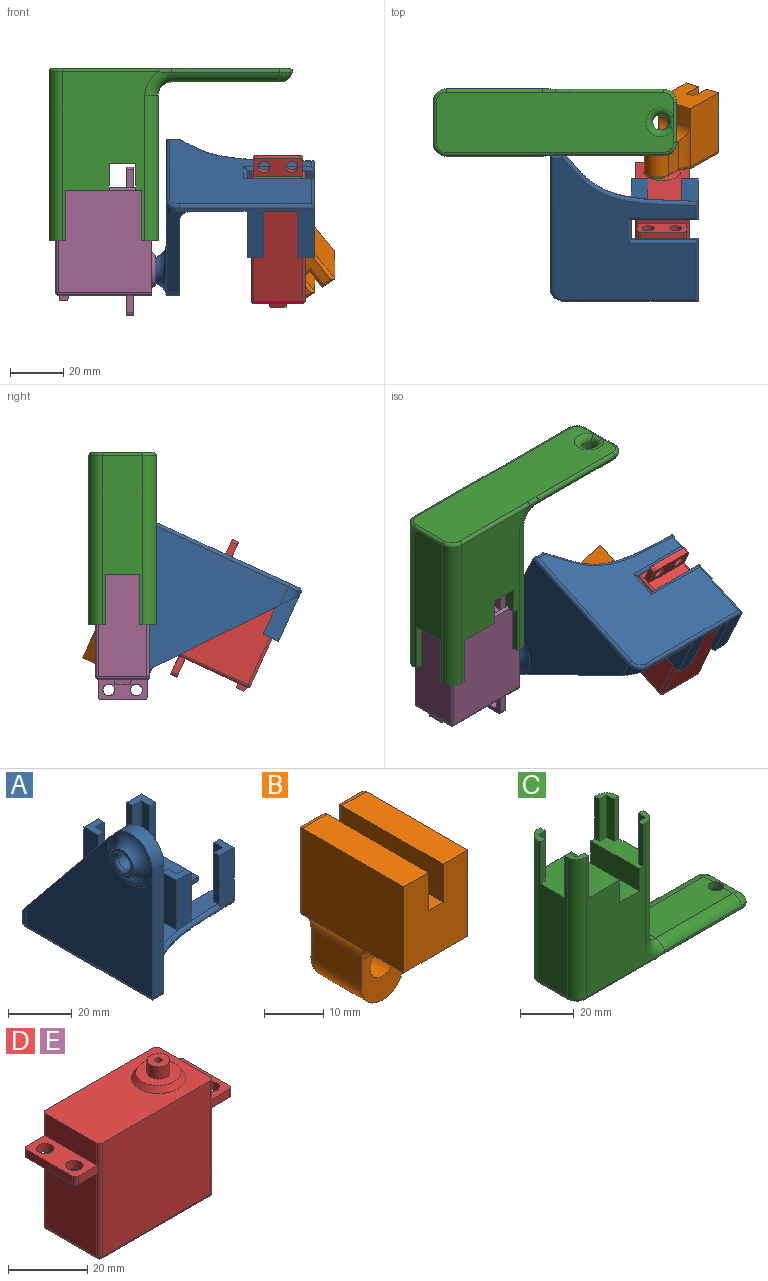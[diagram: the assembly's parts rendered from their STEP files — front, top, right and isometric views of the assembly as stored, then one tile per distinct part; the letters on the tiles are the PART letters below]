
ASSEMBLY  parts=5 mates=3
PART A: 56 faces, bbox 65.1x64.5x63.1 mm
  f0: plane 58.3x53.35mm, normal (0,0,-1), area 2065.8mm2, adj f41,f42,f43,f44,f45,f46,f47,f48
  f1: plane 20.32x7.53mm, normal (1,0,0), area 130.5mm2, adj f2,f33,f34,f35,f39,f41
  f2: plane 52.89x45.73mm, normal (0,0,1), area 1646.4mm2, adj f1,f10,f11,f12,f13,f14,f15,f17
  f3: plane 55.6x45.67mm, normal (0,0.77,0.63), area 351.5mm2, adj f4,f7,f8,f11,f36,f50,f52
  f4: cylinder r=9.53mm len=16.91mm, axis (1,0,0), area 119.4mm2, adj f3,f5,f8,f36
  f5: plane 51.02x7.01mm, normal (0,-1,0), area 249.5mm2, adj f4,f7,f8,f36,f44,f54
  f6: cylinder r=2.92mm len=7.62mm, axis (1,0,0), area 139.9mm2, adj f8,f55
  f7: plane 55.75x52.77mm, normal (-1,0,0), area 1879.7mm2, adj f3,f5,f36,f46,f50
  f8: plane 56.69x54.82mm, normal (1,0,0), area 1806.2mm2, adj f3,f4,f5,f6,f52,f53
  f9: plane 10.16x10.16mm, normal (-1,0,0), area 25.9mm2, adj f36,f55
  f10: plane 25.4x20.32mm, normal (1,0,0), area 153.2mm2, adj f2,f11,f15,f16,f38,f49
  f11: plane 50.8x20.32mm, normal (0,1,0), area 306.5mm2, adj f2,f3,f10,f12,f16,f17,f18,f22
  f12: plane 19.05x2.54mm, normal (-1,0,0), area 48.4mm2, adj f2,f11,f13,f16
  f13: plane 19.05x3.81mm, normal (0,-1,0), area 72.6mm2, adj f2,f12,f14,f16
  f14: plane 19.05x3.81mm, normal (-1,0,0), area 72.6mm2, adj f2,f13,f15,f16
  f15: plane 19.05x2.54mm, normal (0,-1,0), area 48.4mm2, adj f2,f10,f14,f16
  f16: plane 6.35x6.35mm, normal (0,0,1), area 25.8mm2, adj f10,f11,f12,f13,f14,f15
  f17: plane 19.05x2.54mm, normal (1,0,0), area 48.4mm2, adj f2,f11,f21,f22
  f18: plane 19.05x6.35mm, normal (-1,0,0), area 121mm2, adj f2,f11,f19,f22
  f19: plane 19.05x2.54mm, normal (0,-1,0), area 48.4mm2, adj f2,f18,f20,f22
  f20: plane 19.05x3.81mm, normal (1,0,0), area 72.6mm2, adj f2,f19,f21,f22
  f21: plane 19.05x3.81mm, normal (0,-1,0), area 72.6mm2, adj f2,f17,f20,f22
  f22: plane 6.35x6.35mm, normal (0,0,1), area 25.8mm2, adj f11,f17,f18,f19,f20,f21
  f23: plane 19.05x6.35mm, normal (-1,0,0), area 121mm2, adj f2,f24,f28,f29
  f24: plane 19.19x6.4mm, normal (0,-1,0), area 121.1mm2, adj f2,f23,f25,f29,f40
  f25: plane 19.15x2.55mm, normal (1,0,0), area 48.4mm2, adj f2,f24,f26,f29,f40
  f26: plane 19.05x3.81mm, normal (0,1,0), area 72.6mm2, adj f2,f25,f27,f29
  f27: plane 19.05x3.81mm, normal (1,0,0), area 72.6mm2, adj f2,f26,f28,f29
  f28: plane 19.05x2.54mm, normal (0,1,0), area 48.4mm2, adj f2,f23,f27,f29
  f29: plane 6.35x6.35mm, normal (0,0,1), area 25.8mm2, adj f23,f24,f25,f26,f27,f28
  f30: plane 19.05x3.81mm, normal (-1,0,0), area 72.6mm2, adj f2,f31,f34,f35
  f31: plane 19.05x3.81mm, normal (0,1,0), area 72.6mm2, adj f2,f30,f32,f35
  f32: plane 19.84x2.59mm, normal (-1,0,0), area 48.6mm2, adj f2,f31,f33,f35,f40
  f33: plane 20.55x6.58mm, normal (0,-1,0), area 126.9mm2, adj f1,f32,f35,f40
  f34: plane 19.05x2.54mm, normal (0,1,0), area 48.4mm2, adj f1,f2,f30,f35
  f35: plane 6.35x6.35mm, normal (0,0,1), area 25.8mm2, adj f1,f30,f31,f32,f33,f34
  f36: torus R=10mm, axis (1,0,0), area 286.2mm2, adj f3,f4,f5,f7,f9
  f37: plane 8.22x1.27mm, normal (1,0,0), area 10.4mm2, adj f2,f38,f39,f45
  f38: plane 25.4x1.27mm, normal (0,-1,0), area 32.3mm2, adj f2,f10,f37,f47
  f39: plane 25.4x1.27mm, normal (0,1,0), area 32.3mm2, adj f1,f2,f37,f43
  f40: bspline ~54.19x21.19mm, area 95.1mm2, adj f2,f24,f25,f32,f33,f42,f53,f54
  f41: cylinder r=1.27mm len=7.53mm, axis (0,-1,0), area 12.5mm2, adj f0,f1,f42,f43
  f42: bspline ~54.19x21.19mm, area 113.8mm2, adj f0,f40,f41,f44
  f43: cylinder r=1.27mm len=26.67mm, axis (-1,0,0), area 50.7mm2, adj f0,f39,f41,f45
  f44: cylinder r=1.27mm len=5.08mm, axis (-1,0,0), area 8.3mm2, adj f0,f5,f42,f46
  f45: cylinder r=1.27mm len=10.76mm, axis (0,1,0), area 18.9mm2, adj f0,f37,f43,f47
  f46: cylinder r=1.27mm len=55.75mm, axis (0,1,0), area 110mm2, adj f0,f7,f44,f51
  f47: cylinder r=1.27mm len=26.67mm, axis (1,0,0), area 50.7mm2, adj f0,f38,f45,f49
  f48: cylinder r=1.27mm len=50.8mm, axis (1,0,0), area 100.1mm2, adj f0,f11,f49,f51
  f49: cylinder r=1.27mm len=25.4mm, axis (0,-1,0), area 48.1mm2, adj f0,f10,f47,f48
  f50: cylinder r=5.08mm len=7.5mm, axis (0,0,1), area 28.2mm2, adj f3,f7,f11,f51
  f51: torus R=3.81mm, axis (0,0,1), area 14.5mm2, adj f0,f46,f48,f50
  f52: cylinder r=5.08mm len=52.89mm, axis (0,-1,0), area 405.5mm2, adj f2,f3,f8,f53
  f53: bspline ~9.52x5.7mm, area 41.8mm2, adj f8,f40,f52,f54
  f54: bspline ~4.35x3.03mm, area 3.8mm2, adj f5,f40,f53
  f55: torus R=4.19mm, axis (-1,0,0), area 42.4mm2, adj f6,f9
PART B: 34 faces, bbox 15.2x25.4x33.9 mm
  f0: plane 7.62x4.86mm, normal (0,1,0), area 17.4mm2, adj f23,f25,f27,f29
  f1: plane 24.13x17.78mm, normal (1,0,0), area 429mm2, adj f2,f8,f9,f16,f26
  f2: plane 24.13x5.87mm, normal (0,0,1), area 141.7mm2, adj f1,f3,f9,f24
  f3: plane 24.13x7.87mm, normal (-1,0,0), area 190mm2, adj f2,f4,f9,f22
  f4: plane 24.13x3.49mm, normal (0,0,1), area 84.3mm2, adj f3,f5,f9,f20
  f5: plane 24.13x7.87mm, normal (1,0,0), area 190mm2, adj f4,f6,f9,f18
  f6: plane 24.13x5.87mm, normal (0,0,1), area 141.7mm2, adj f5,f7,f9,f17
  f7: plane 24.13x17.78mm, normal (-1,0,0), area 429mm2, adj f6,f8,f9,f15,f19
  f8: plane 15.24x7.62mm, normal (0,0,-1), area 116.1mm2, adj f1,f7,f9,f31,f32,f33
  f9: plane 17.78x15.24mm, normal (0,-1,0), area 243.5mm2, adj f1,f2,f3,f4,f5,f6,f7,f8
  f10: plane 22.64x12.7mm, normal (0,1,0), area 199.8mm2, adj f17,f18,f19,f20,f21,f22,f23,f24
  f11: plane 11.48x6.27mm, normal (-1,0,0), area 71.7mm2, adj f14,f15,f23,f30,f31
  f12: plane 11.48x6.27mm, normal (1,0,0), area 71.7mm2, adj f14,f16,f27,f30,f33
  f13: cylinder r=2.92mm len=11.43mm, axis (0,1,0), area 209.8mm2, adj f14,f25,f32
  f14: plane 10.67x10.16mm, normal (0,-1,0), area 70.7mm2, adj f11,f12,f13,f30,f31,f33
  f15: cylinder r=5.08mm len=16.51mm, axis (0,-1,0), area 68.7mm2, adj f7,f11,f21,f31
  f16: cylinder r=5.08mm len=16.51mm, axis (0,-1,0), area 68.7mm2, adj f1,f12,f28,f33
  f17: cylinder r=1.27mm len=5.87mm, axis (-1,0,0), area 9.9mm2, adj f6,f10,f18,f19
  f18: cylinder r=1.27mm len=9.14mm, axis (0,0,1), area 15.7mm2, adj f5,f10,f17,f20
  f19: cylinder r=1.27mm len=17.78mm, axis (0,0,-1), area 33.9mm2, adj f7,f10,f17,f21
  f20: cylinder r=1.27mm len=6.03mm, axis (-1,0,0), area 8.8mm2, adj f4,f10,f18,f22
  f21: torus R=6.35mm, axis (0,-1,0), area 10.9mm2, adj f10,f15,f19,f23
  f22: cylinder r=1.27mm len=9.14mm, axis (0,0,-1), area 15.7mm2, adj f3,f10,f20,f24
  f23: cylinder r=1.27mm len=6.27mm, axis (0,0,-1), area 12.1mm2, adj f0,f10,f11,f21,f25,f29
  f24: cylinder r=1.27mm len=5.87mm, axis (-1,0,0), area 9.9mm2, adj f2,f10,f22,f26
  f25: torus R=4.19mm, axis (0,-1,0), area 41.5mm2, adj f0,f10,f13,f23,f27
  f26: cylinder r=1.27mm len=17.78mm, axis (0,0,1), area 33.9mm2, adj f1,f10,f24,f28
  f27: cylinder r=1.27mm len=6.27mm, axis (0,0,1), area 12.1mm2, adj f0,f10,f12,f25,f28,f29
  f28: torus R=6.35mm, axis (0,-1,0), area 10.9mm2, adj f10,f16,f26,f27
  f29: torus R=3.81mm, axis (0,-1,0), area 28.9mm2, adj f0,f23,f27,f30
  f30: cylinder r=5.08mm len=11.43mm, axis (0,1,0), area 182.4mm2, adj f11,f12,f14,f29
  f31: cylinder r=5.08mm len=6.77mm, axis (-1,0,0), area 42.3mm2, adj f8,f11,f14,f15,f32
  f32: bspline ~5.24x5.23mm, area 13.4mm2, adj f8,f13,f31,f33
  f33: cylinder r=5.08mm len=6.77mm, axis (-1,0,0), area 42.3mm2, adj f8,f12,f14,f16,f32
PART C: 58 faces, bbox 92.5x26.2x69.6 mm
  f0: cylinder r=5.08mm len=15.24mm, axis (0,-1,0), area 89mm2, adj f1,f41,f42,f53,f55
  f1: plane 40.64x15.24mm, normal (0,0,1), area 598.8mm2, adj f0,f33,f36,f38,f55
  f2: plane 63.61x36.23mm, normal (0,-1,0), area 1339.6mm2, adj f3,f4,f14,f18,f22,f23,f29,f30
  f3: plane 25.4x22.56mm, normal (0,0,1), area 521.5mm2, adj f2,f6,f7,f9,f10,f11,f12,f14
  f4: plane 25.4x8.43mm, normal (0,0,1), area 162.4mm2, adj f2,f7,f8,f19,f20,f21,f22,f24
  f5: plane 89.19x22.86mm, normal (0,0,-1), area 1915mm2, adj f43,f44,f45,f46,f47,f48,f49,f50
  f6: plane 63.61x15.24mm, normal (-1,0,0), area 727.5mm2, adj f3,f12,f13,f17,f18,f39,f40,f44
  f7: plane 63.61x36.23mm, normal (0,1,0), area 1339.6mm2, adj f3,f4,f11,f13,f24,f28,f29,f30
  f8: plane 54.72x15.24mm, normal (1,0,0), area 592.1mm2, adj f4,f19,f23,f27,f28,f32,f35,f36
  f9: plane 19.05x3.81mm, normal (1,0,0), area 72.6mm2, adj f3,f10,f12,f13
  f10: plane 19.05x3.81mm, normal (0,-1,0), area 72.6mm2, adj f3,f9,f11,f13
  f11: plane 19.05x2.54mm, normal (1,0,0), area 48.4mm2, adj f3,f7,f10,f13
  f12: plane 19.05x2.54mm, normal (0,-1,0), area 48.4mm2, adj f3,f6,f9,f13
  f13: plane 6.35x6.35mm, normal (0,0,1), area 20.3mm2, adj f6,f7,f9,f10,f11,f12,f39
  f14: plane 19.05x2.54mm, normal (1,0,0), area 48.4mm2, adj f2,f3,f15,f18
  f15: plane 19.05x3.81mm, normal (0,1,0), area 72.6mm2, adj f3,f14,f16,f18
  f16: plane 19.05x3.81mm, normal (1,0,0), area 72.6mm2, adj f3,f15,f17,f18
  f17: plane 19.05x2.54mm, normal (0,1,0), area 48.4mm2, adj f3,f6,f16,f18
  f18: plane 6.35x6.35mm, normal (0,0,1), area 20.3mm2, adj f2,f6,f14,f15,f16,f17,f40
  f19: plane 19.05x2.54mm, normal (0,1,0), area 48.4mm2, adj f4,f8,f20,f23
  f20: plane 19.05x3.81mm, normal (-1,0,0), area 72.6mm2, adj f4,f19,f21,f23
  f21: plane 19.05x3.81mm, normal (0,1,0), area 72.6mm2, adj f4,f20,f22,f23
  f22: plane 19.05x2.54mm, normal (-1,0,0), area 48.4mm2, adj f2,f4,f21,f23
  f23: plane 6.35x6.35mm, normal (0,0,1), area 20.3mm2, adj f2,f8,f19,f20,f21,f22,f35
  f24: plane 19.05x2.54mm, normal (-1,0,0), area 48.4mm2, adj f4,f7,f25,f28
  f25: plane 19.05x3.81mm, normal (0,-1,0), area 72.6mm2, adj f4,f24,f26,f28
  f26: plane 19.05x3.81mm, normal (-1,0,0), area 72.6mm2, adj f4,f25,f27,f28
  f27: plane 19.05x2.54mm, normal (0,-1,0), area 48.4mm2, adj f4,f8,f26,f28
  f28: plane 6.35x6.35mm, normal (0,0,1), area 20.3mm2, adj f7,f8,f24,f25,f26,f27,f32
  f29: plane 25.4x10.16mm, normal (1,0,0), area 258.1mm2, adj f2,f3,f7,f31
  f30: plane 25.4x10.16mm, normal (-1,0,0), area 258.1mm2, adj f2,f4,f7,f31
  f31: plane 25.4x10.16mm, normal (0,0,1), area 258.1mm2, adj f2,f7,f29,f30
  f32: cylinder r=5.08mm len=54.72mm, axis (0,0,-1), area 436.7mm2, adj f7,f8,f28,f34
  f33: cylinder r=5.08mm len=40.64mm, axis (-1,0,0), area 254.1mm2, adj f1,f34,f42,f52
  f34: torus R=10.16mm, axis (0,-1,0), area 82.6mm2, adj f7,f32,f33,f36,f50
  f35: cylinder r=5.08mm len=54.72mm, axis (0,0,1), area 436.7mm2, adj f2,f8,f23,f37
  f36: cylinder r=5.08mm len=15.24mm, axis (0,1,0), area 121.6mm2, adj f1,f8,f34,f37
  f37: torus R=10.16mm, axis (0,-1,0), area 82.6mm2, adj f2,f35,f36,f38,f47
  f38: cylinder r=5.08mm len=40.64mm, axis (1,0,0), area 254.1mm2, adj f1,f37,f41,f49
  f39: cylinder r=5.08mm len=63.61mm, axis (0,0,-1), area 507.6mm2, adj f6,f7,f13,f46
  f40: cylinder r=5.08mm len=63.61mm, axis (0,0,1), area 507.6mm2, adj f2,f6,f18,f43
  f41: sphere r=5.08mm, area 27mm2, adj f0,f38,f51
  f42: sphere r=5.08mm, area 27mm2, adj f0,f33,f54
  f43: torus R=3.81mm, axis (0,0,-1), area 14.5mm2, adj f5,f40,f44,f45
  f44: cylinder r=1.27mm len=15.24mm, axis (0,-1,0), area 30.4mm2, adj f5,f6,f43,f46
  f45: cylinder r=1.27mm len=36.23mm, axis (-1,0,0), area 72.3mm2, adj f2,f5,f43,f47
  f46: torus R=3.81mm, axis (0,0,-1), area 14.5mm2, adj f5,f39,f44,f48
  f47: bspline ~7.2x1.8mm, area 11.1mm2, adj f5,f37,f45,f49
  f48: cylinder r=1.27mm len=36.23mm, axis (1,0,0), area 72.3mm2, adj f5,f7,f46,f50
  f49: cylinder r=1.27mm len=40.64mm, axis (1,0,0), area 98.6mm2, adj f5,f38,f47,f51
  f50: bspline ~7.2x1.8mm, area 11.1mm2, adj f5,f34,f48,f52
  f51: torus R=3.59mm, axis (0,0,-1), area 17.1mm2, adj f5,f41,f49,f53
  f52: cylinder r=1.27mm len=40.64mm, axis (-1,0,0), area 98.6mm2, adj f5,f33,f50,f54
  f53: cylinder r=1.27mm len=15.24mm, axis (0,-1,0), area 37mm2, adj f0,f5,f51,f54,f57
  f54: torus R=3.59mm, axis (0,0,-1), area 17.1mm2, adj f5,f42,f52,f53
  f55: cylinder r=2.92mm len=5.84mm, axis (0,0,-1), area 46.6mm2, adj f0,f1,f56,f57
  f56: torus R=5.46mm, axis (0,0,-1), area 81.9mm2, adj f5,f55,f57
  f57: bspline ~5.93x2.84mm, area 12.5mm2, adj f53,f55,f56
PART D: 49 faces, bbox 55.9x20.3x41.6 mm
  f0: plane 18.29x6.86mm, normal (-1,0,0), area 125.4mm2, adj f6,f21,f33,f38
  f1: plane 18.29x6.86mm, normal (1,0,0), area 125.4mm2, adj f6,f30,f35,f44
  f2: plane 25.65x18.29mm, normal (1,0,0), area 446.3mm2, adj f9,f10,f11,f12,f29,f35,f41,f44
  f3: plane 38.61x35.05mm, normal (0,-1,0), area 1353.3mm2, adj f6,f38,f42,f44
  f4: plane 38.61x35.05mm, normal (0,1,0), area 1353.3mm2, adj f6,f33,f35,f36
  f5: plane 25.65x18.29mm, normal (-1,0,0), area 469.2mm2, adj f20,f33,f37,f38
  f6: plane 40.64x20.32mm, normal (0,0,1), area 677.2mm2, adj f0,f1,f3,f4,f32,f33,f35,f38
  f7: plane 38.61x18.29mm, normal (0,0,-1), area 706.1mm2, adj f36,f37,f41,f42
  f8: plane 6.02x3.07mm, normal (1,0,0), area 18.5mm2, adj f9,f10,f11,f12
  f9: plane 6.35x1.91mm, normal (0.14,0,0.99), area 11.9mm2, adj f2,f8,f10,f12
  f10: plane 3.61x1.91mm, normal (0.09,-1,0), area 6.4mm2, adj f2,f8,f9,f11
  f11: plane 6.35x1.91mm, normal (0.14,0,-0.99), area 11.9mm2, adj f2,f8,f10,f12
  f12: plane 3.61x1.91mm, normal (0.09,1,0), area 6.4mm2, adj f2,f8,f9,f11
  f13: plane 6.61x2.54mm, normal (0,1,0), area 16.8mm2, adj f14,f20,f21,f33
  f14: cylinder r=1.02mm len=2.54mm, axis (0,0,1), area 4.1mm2, adj f13,f15,f20,f21
  f15: plane 16.51x2.54mm, normal (-1,0,0), area 41.9mm2, adj f14,f16,f20,f21
  f16: cylinder r=1.02mm len=2.54mm, axis (0,0,1), area 4.1mm2, adj f15,f18,f20,f21
  f17: cylinder r=2.22mm len=4.45mm, axis (0,0,1), area 35.5mm2, adj f20,f21
  f18: plane 6.61x2.54mm, normal (0,-1,0), area 16.8mm2, adj f16,f20,f21,f38
  f19: cylinder r=2.22mm len=4.45mm, axis (0,0,1), area 35.5mm2, adj f20,f21
  f20: plane 18.54x7.63mm, normal (0,0,-1), area 109.8mm2, adj f5,f13,f14,f15,f16,f17,f18,f19
  f21: plane 18.54x7.63mm, normal (0,0,1), area 109.8mm2, adj f0,f13,f14,f15,f16,f17,f18,f19
  f22: plane 6.61x2.54mm, normal (0,1,0), area 16.8mm2, adj f26,f29,f30,f35
  f23: plane 6.61x2.54mm, normal (0,-1,0), area 16.8mm2, adj f24,f29,f30,f44
  f24: cylinder r=1.02mm len=2.54mm, axis (0,0,1), area 4.1mm2, adj f23,f25,f29,f30
  f25: plane 16.51x2.54mm, normal (1,0,0), area 41.9mm2, adj f24,f26,f29,f30
  f26: cylinder r=1.02mm len=2.54mm, axis (0,0,1), area 4.1mm2, adj f22,f25,f29,f30
  f27: cylinder r=2.22mm len=4.45mm, axis (0,0,1), area 35.5mm2, adj f29,f30
  f28: cylinder r=2.22mm len=4.45mm, axis (0,0,1), area 35.5mm2, adj f29,f30
  f29: plane 18.54x7.63mm, normal (0,0,-1), area 109.8mm2, adj f2,f22,f23,f24,f25,f26,f27,f28
  f30: plane 18.54x7.63mm, normal (0,0,1), area 109.8mm2, adj f1,f22,f23,f24,f25,f26,f27,f28
  f31: plane 11.4x11.4mm, normal (0,0,1), area 76mm2, adj f32,f46
  f32: cone r=6.86mm half-angle=35deg, axis (0,0,-1), area 79.5mm2, adj f6,f31
  f33: cylinder r=1.02mm len=35.05mm, axis (0,0,-1), area 55.6mm2, adj f0,f4,f5,f6,f13,f20,f21,f34
  f34: sphere r=1.02mm, area 1.6mm2, adj f33,f36,f37
  f35: cylinder r=1.02mm len=35.05mm, axis (0,0,1), area 55.6mm2, adj f1,f2,f4,f6,f22,f29,f30,f39
  f36: cylinder r=1.02mm len=38.61mm, axis (-1,0,0), area 61.6mm2, adj f4,f7,f34,f39
  f37: cylinder r=1.02mm len=18.29mm, axis (0,-1,0), area 29.2mm2, adj f5,f7,f34,f40
  f38: cylinder r=1.02mm len=35.05mm, axis (0,0,1), area 55.6mm2, adj f0,f3,f5,f6,f18,f20,f21,f40
  f39: sphere r=1.02mm, area 1.6mm2, adj f35,f36,f41
  f40: sphere r=1.02mm, area 1.6mm2, adj f37,f38,f42
  f41: cylinder r=1.02mm len=18.29mm, axis (0,1,0), area 29.2mm2, adj f2,f7,f39,f43
  f42: cylinder r=1.02mm len=38.61mm, axis (1,0,0), area 61.6mm2, adj f3,f7,f40,f43
  f43: sphere r=1.02mm, area 1.6mm2, adj f41,f42,f44
  f44: cylinder r=1.02mm len=35.05mm, axis (0,0,-1), area 55.6mm2, adj f1,f2,f3,f6,f23,f29,f30,f43
  f45: cylinder r=0.94mm len=3.86mm, axis (0,0,-1), area 22.8mm2, adj f47,f48
  f46: cylinder r=2.88mm len=5.77mm, axis (0,0,-1), area 69.9mm2, adj f31,f47
  f47: plane 5.77x5.77mm, normal (0,0,1), area 23.3mm2, adj f45,f46
  f48: plane 1.88x1.88mm, normal (0,0,1), area 2.8mm2, adj f45
PART E: same geometry as D
PLACE A rot(axis=(-1,0,0),155.4deg) t=(19.45,-34.72,21.36)mm
PLACE B rot(axis=(-0.95,0.07,-0.31),156.6deg) t=(28.43,-36.13,25.36)mm
PLACE C rot(axis=(1,0,0),180deg) t=(17.8,-34.72,21.14)mm fixed
PLACE D rot(axis=(-0.48,0.48,0.74),107deg) t=(18.44,-90.94,26.97)mm
PLACE E rot(axis=(0,1,0),90deg) t=(-65.25,-34.72,32.2)mm
MATE fastened D.f33 <-> A.f21  axis (0,-0.91,-0.42) through (9.29,-98.99,44.52)mm
MATE revolute B.f13 <-> D.f32  axis (0,-0.91,-0.42) through (18.44,-52.13,32.83)mm
MATE fastened C.f26 <-> E.f6  axis (-1,0,0) through (-29.19,-44.88,51.51)mm
